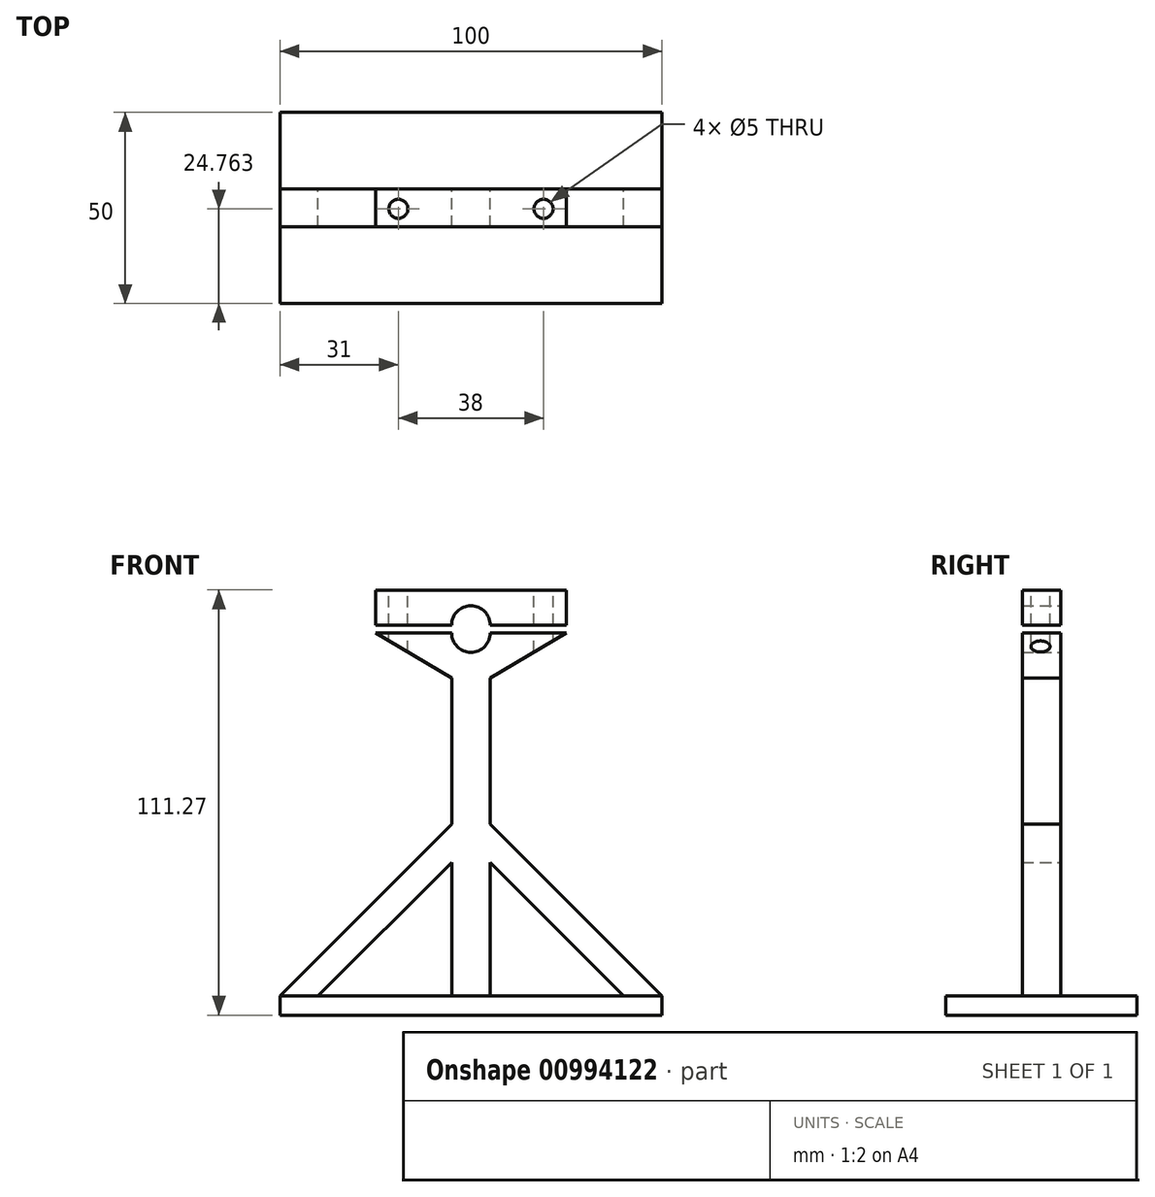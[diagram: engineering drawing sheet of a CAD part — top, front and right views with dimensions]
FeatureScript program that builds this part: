
annotation { "Feature Type Name" : "Feature", "Feature Type Description" : "" }
export const myFeature = defineFeature(function(context is Context, id is Id, definition is map)
    precondition{}
    {
        {
            var Q0;
            Q0=qCreatedBy(makeId("Front.planeOp"),FACE);
            var sketch = newSketch(context, id + "F0", { "sketchPlane" : qUnion([Q0])});
            skLineSegment(sketch, "E0.bottom", {"start": v(-25, 50) * mm, "end": v(-5.05, 50) * mm});
            skLineSegment(sketch, "E0.top", {"start": v(-50, -50) * mm, "end": v(50, -50) * mm});
            skLineSegment(sketch, "E0.left", {"start": v(-50, 0) * mm, "end": v(-50, -50) * mm});
            skLineSegment(sketch, "E0.right", {"start": v(50, -45) * mm, "end": v(50, -50) * mm});
            skPoint(sketch, "E0.middle", {"position": v(0, 0) * mm});
            skLineSegment(sketch, "E1", {"start": v(40, -45) * mm, "end": v(5, -45) * mm});
            skLineSegment(sketch, "E2", {"start": v(-40, -45) * mm, "end": v(-5, -45) * mm});
            skLineSegment(sketch, "E3", {"start": v(5, -45) * mm, "end": v(5, -10) * mm});
            skLineSegment(sketch, "E4", {"start": v(-5, -45) * mm, "end": v(-5, -10) * mm});
            skLineSegment(sketch, "E5", {"start": v(0, 0) * mm, "end": v(-50, 0) * mm, "construction": true});
            skLineSegment(sketch, "E6", {"start": v(0, 0) * mm, "end": v(50, 0) * mm, "construction": true});
            skLineSegment(sketch, "E7", {"start": v(-5, 0) * mm, "end": v(-50, -45) * mm});
            skLineSegment(sketch, "E8", {"start": v(-5, -10) * mm, "end": v(-40, -45) * mm});
            skLineSegment(sketch, "E9", {"start": v(5, 0) * mm, "end": v(50, -45) * mm});
            skLineSegment(sketch, "E10", {"start": v(5, -10) * mm, "end": v(40, -45) * mm});
            skLineSegment(sketch, "E11", {"start": v(5, 38.26) * mm, "end": v(25, 50) * mm});
            skLineSegment(sketch, "E12", {"start": v(-5, 38.26) * mm, "end": v(-25, 50) * mm});
            skPoint(sketch, "E13.end.orphan", {"position": v(0, 50) * mm});
            skPoint(sketch, "E14.orphan", {"position": v(-5, 50) * mm});
            skPoint(sketch, "E15.orphan", {"position": v(5, 50) * mm});
            skLineSegment(sketch, "E16.trimOffspring", {"start": v(-5, 0) * mm, "end": v(-5, 38.26) * mm});
            skLineSegment(sketch, "E17.trimOffspring", {"start": v(5, 0) * mm, "end": v(5, 38.26) * mm});
            skPoint(sketch, "E18.end.orphan", {"position": v(0, -45) * mm});
            skLineSegment(sketch, "E19.trimOffspring", {"start": v(-5, -45) * mm, "end": v(-40, -45) * mm});
            skPoint(sketch, "E20.orphan", {"position": v(-50, 50) * mm});
            skPoint(sketch, "E21.orphan", {"position": v(50, 50) * mm});
            skLineSegment(sketch, "E22", {"start": v(25, 52.1) * mm, "end": v(25, 61.27) * mm});
            skLineSegment(sketch, "E23", {"start": v(25, 61.27) * mm, "end": v(-25, 61.27) * mm});
            skLineSegment(sketch, "E24", {"start": v(-25, 52.1) * mm, "end": v(-25, 61.27) * mm});
            skLineSegment(sketch, "E25", {"start": v(-5.05, 50) * mm, "end": v(-5, 50) * mm});
            skLineSegment(sketch, "E26", {"start": v(5.05, 50) * mm, "end": v(25, 50) * mm});
            skArc(sketch, "E27", {"start": v(5.05, 52.1) * mm, "mid": v(0, 57.15) * mm, "end": v(-5.05, 52.1) * mm});
            skArc(sketch, "E28", {"start": v(-5.05, 50) * mm, "mid": v(0, 44.95) * mm, "end": v(5.05, 50) * mm});
            skLineSegment(sketch, "E29", {"start": v(25, 52.1) * mm, "end": v(5.05, 52.1) * mm});
            skLineSegment(sketch, "E30", {"start": v(-5.05, 52.1) * mm, "end": v(-25, 52.1) * mm});
            skLineSegment(sketch, "E31.trimOffspring", {"start": v(5, 50) * mm, "end": v(5.05, 50) * mm});
            skSolve(sketch);
        }
        {
            var Q0;
            {var subQ7=sQuery(id+"F0.wireOp",EDGE,"E0.top");Q0=makeQuery(id+"F0.imprint","IMPRINT",FACE,{"disambiguationData":[TD([[makeQuery(id+"F0.imprint","IMPRINT",EDGE,{"derivedFrom":subQ7}),1.0]])]});}
            var Q1;
            {var subQ4=sQuery(id+"F0.wireOp",EDGE,"jqdFN3Wo-HjUL-DWxb-vY1L-fUWDQ7hTO9kh");Q1=makeQuery(id+"F0.imprint","IMPRINT",FACE,{"disambiguationData":[TD([[makeQuery(id+"F0.imprint","IMPRINT",EDGE,{"derivedFrom":subQ4}),1.0]])]});}
            var Q2;
            Q2=makeQuery(id+"F0.imprint","IMPRINT",FACE,{"disambiguationData":[TD([[makeQuery(id+"F0.imprint","IMPRINT",EDGE,{"derivedFrom":sQuery(id+"F0.wireOp",EDGE,"E22")}),1.0]])]});
            extrude(context, id + "F1", {"entities" : qUnion([Q0, Q1, Q2]), "depth" : 10 * mm, "offsetDistance" : 25 * mm});
        }
        {
            var Q0;
            Q0=qCreatedBy(makeId("Top.planeOp"),FACE);
            cPlane(context, id + "F2", {"entities" : qUnion([Q0]), "cplaneType" : CPlaneType.OFFSET, "offset" : 61.5 * mm, "width" : 150 * mm, "height" : 150 * mm});
        }
        {
            var Q0;
            Q0=qCreatedBy(id+"F2.planeOp",FACE);
            var sketch = newSketch(context, id + "F3", { "sketchPlane" : qUnion([Q0])});
            skPoint(sketch, "E32", {"position": v(-19, -5.24) * mm});
            skPoint(sketch, "E33", {"position": v(19, -5.24) * mm});
            skCircle(sketch, "E34", {"center": v(-19, -5.24) * mm, "radius": 2.5 * mm});
            skCircle(sketch, "E35", {"center": v(19, -5.24) * mm, "radius": 2.5 * mm});
            skSolve(sketch);
        }
        {
            var Q0;
            Q0 = qSketchRegion(id + "F3", true);
            extrude(context, id + "F4", {"entities" : qUnion([Q0]), "operationType" : NewBodyOperationType.REMOVE, "oppositeDirection" : true, "depth" : 25 * mm, "offsetDistance" : 25 * mm});
        }
        {
            var Q0;
            Q0=makeQuery(id+"F1.opExtrude","SWEPT_FACE",FACE,{"disambiguationData":[OSD([sQuery(id+"F0.wireOp",EDGE,"E0.top")])]});
            var sketch = newSketch(context, id + "F5", { "sketchPlane" : qUnion([Q0])});
            skLineSegment(sketch, "E36.bottom", {"start": v(50, 0) * mm, "end": v(-50, 0) * mm});
            skLineSegment(sketch, "E36.top", {"start": v(50, -20) * mm, "end": v(-50, -20) * mm});
            skLineSegment(sketch, "E36.left", {"start": v(50, 0) * mm, "end": v(50, -20) * mm});
            skLineSegment(sketch, "E36.right", {"start": v(-50, 0) * mm, "end": v(-50, -20) * mm});
            skLineSegment(sketch, "E37.bottom", {"start": v(50, 10) * mm, "end": v(-50, 10) * mm});
            skLineSegment(sketch, "E37.top", {"start": v(50, 30) * mm, "end": v(-50, 30) * mm});
            skLineSegment(sketch, "E37.left", {"start": v(50, 10) * mm, "end": v(50, 30) * mm});
            skLineSegment(sketch, "E37.right", {"start": v(-50, 10) * mm, "end": v(-50, 30) * mm});
            skSolve(sketch);
        }
        {
            var Q0;
            Q0 = qSketchRegion(id + "F5", true);
            extrude(context, id + "F6", {"entities" : qUnion([Q0]), "operationType" : NewBodyOperationType.ADD, "oppositeDirection" : true, "depth" : 5 * mm, "hasOffset" : true, "offsetDistance" : 20 * mm});
        }
    });
